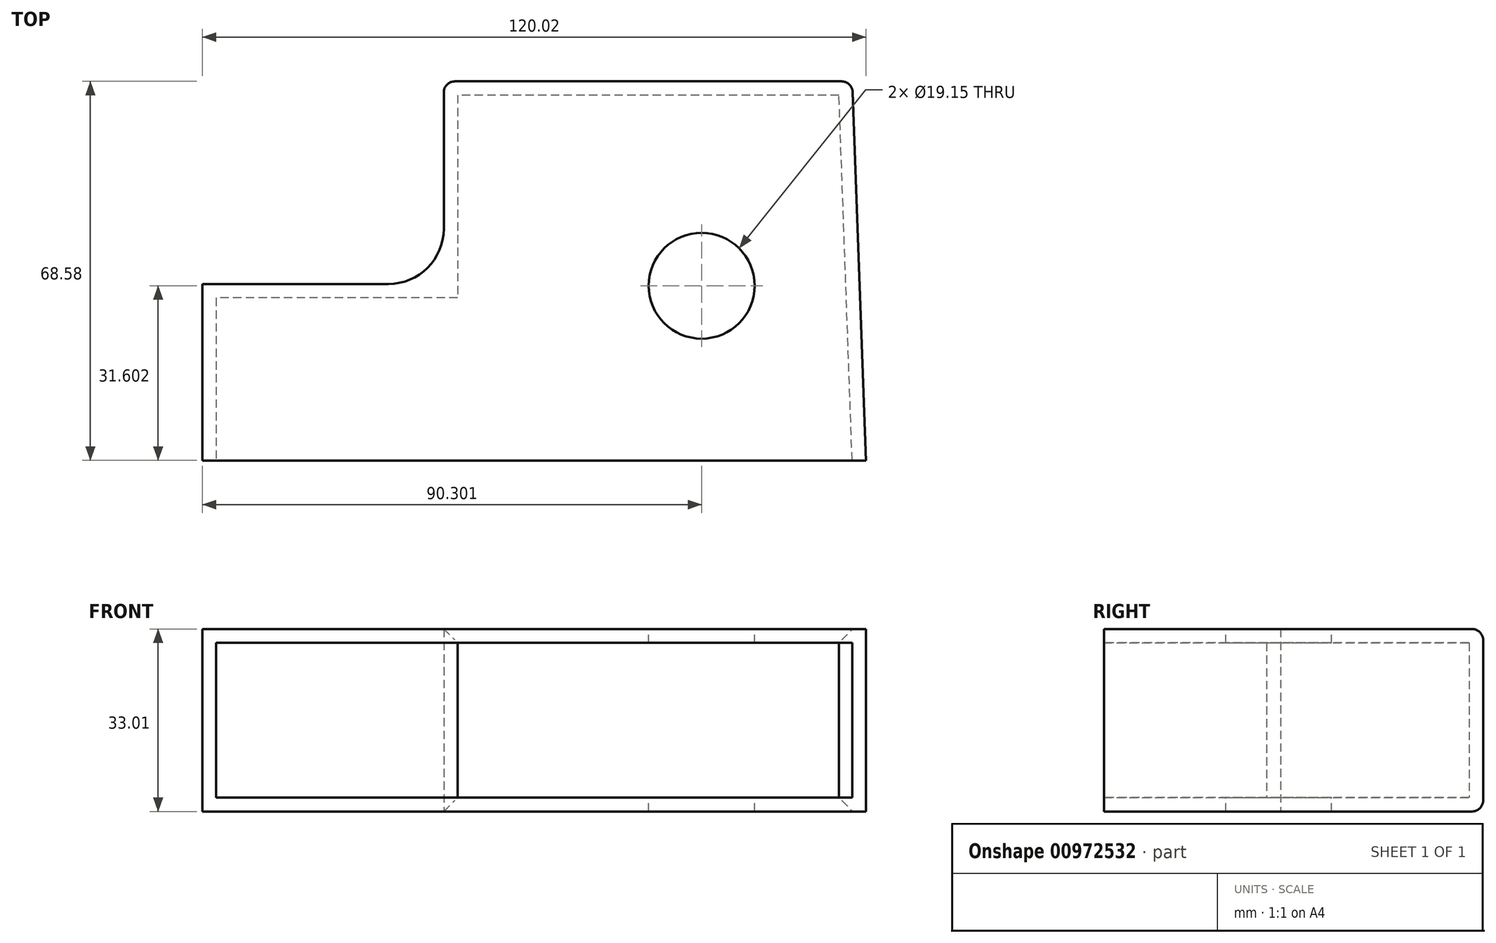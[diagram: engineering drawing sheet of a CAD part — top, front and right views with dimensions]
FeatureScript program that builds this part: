
annotation { "Feature Type Name" : "Feature", "Feature Type Description" : "" }
export const myFeature = defineFeature(function(context is Context, id is Id, definition is map)
    precondition{}
    {
        {
            var Q0;
            Q0=qCreatedBy(makeId("Top.planeOp"),FACE);
            var sketch = newSketch(context, id + "F0", { "sketchPlane" : qUnion([Q0])});
            skLineSegment(sketch, "E0", {"start": v(60.37, 61.9) * mm, "end": v(90.28, 27.23) * mm});
            skLineSegment(sketch, "E1", {"start": v(60.37, 61.9) * mm, "end": v(60.37, 27.23) * mm});
            skLineSegment(sketch, "E2", {"start": v(60.37, 27.23) * mm, "end": v(-13.52, 27.23) * mm});
            skLineSegment(sketch, "E3", {"start": v(-13.52, 27.23) * mm, "end": v(-13.52, -9.42) * mm});
            skLineSegment(sketch, "E4", {"start": v(-13.52, -9.42) * mm, "end": v(-57.18, -9.42) * mm});
            skLineSegment(sketch, "E5", {"start": v(-57.18, -9.42) * mm, "end": v(-57.18, -41.35) * mm});
            skLineSegment(sketch, "E6", {"start": v(-57.18, -41.35) * mm, "end": v(62.84, -41.35) * mm});
            skLineSegment(sketch, "E7", {"start": v(62.84, -41.35) * mm, "end": v(60.37, 27.23) * mm});
            skSolve(sketch);
        }
        {
            var Q0;
            Q0=makeQuery(id+"F0.imprint","IMPRINT",FACE,{"disambiguationData":[TD([[makeQuery(id+"F0.imprint","IMPRINT",EDGE,{"derivedFrom":sQuery(id+"F0.wireOp",EDGE,"E2")}),1.0]])]});
            extrude(context, id + "F1", {"entities" : qUnion([Q0]), "depth" : 33 * mm, "offsetDistance" : 25 * mm});
        }
        {
            var Q0;
            Q0=makeQuery(id+"F1.opExtrude","CAP_FACE",FACE,{"disambiguationData":[OSD([sQuery(id+"F0.wireOp",EDGE,"E2"),sQuery(id+"F0.wireOp",EDGE,"E3"),sQuery(id+"F0.wireOp",EDGE,"E4"),sQuery(id+"F0.wireOp",EDGE,"E5"),sQuery(id+"F0.wireOp",EDGE,"E6"),sQuery(id+"F0.wireOp",EDGE,"E7")])],"isStart":false});
            var sketch = newSketch(context, id + "F2", { "sketchPlane" : qUnion([Q0])});
            skCircle(sketch, "E8", {"center": v(33.12, -9.75) * mm, "radius": 9.57 * mm});
            skSolve(sketch);
        }
        {
            var Q0;
            Q0=makeQuery(id+"F1.opExtrude","SWEPT_FACE",FACE,{"disambiguationData":[OSD([sQuery(id+"F0.wireOp",EDGE,"E2")])]});
            fillet(context, id + "F3", {"entities" : qUnion([Q0]), "radius" : 2 * mm, "tangentPropagation" : true, "allowEdgeOverflow" : false});
        }
        {
            var Q0;
            Q0=makeQuery(id+"F1.opExtrude","SWEPT_FACE",FACE,{"disambiguationData":[OSD([sQuery(id+"F0.wireOp",EDGE,"E6")])]});
            shell(context, id + "F4", {"entities" : qUnion([Q0]), "thickness" : 2.5 * mm});
        }
        {
            var Q0;
            Q0=makeQuery(id+"F1.opExtrude","SWEPT_EDGE",EDGE,{"disambiguationData":[OSD([sQuery(id+"F0.wireOp",EDGE,"E3"),sQuery(id+"F0.wireOp",EDGE,"E4")])]});
            fillet(context, id + "F5", {"entities" : qUnion([Q0]), "radius" : 10 * mm, "tangentPropagation" : true, "allowEdgeOverflow" : false});
        }
        {
            var Q0;
            Q0 = qSketchRegion(id + "F2", true);
            extrude(context, id + "F6", {"entities" : qUnion([Q0]), "operationType" : NewBodyOperationType.REMOVE, "oppositeDirection" : true, "depth" : 66.11 * mm, "offsetDistance" : 25 * mm});
        }
    });
